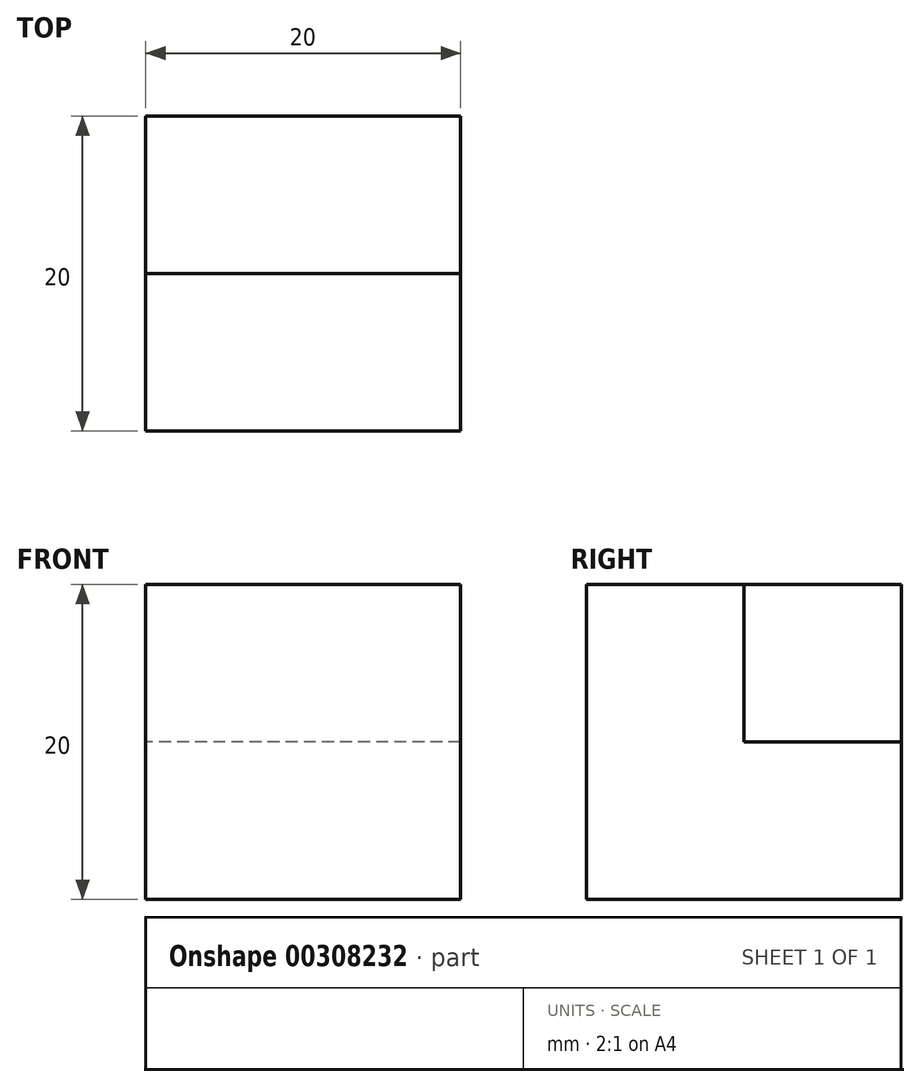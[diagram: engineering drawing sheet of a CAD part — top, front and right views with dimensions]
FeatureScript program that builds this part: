
annotation { "Feature Type Name" : "Feature", "Feature Type Description" : "" }
export const myFeature = defineFeature(function(context is Context, id is Id, definition is map)
    precondition{}
    {
        {
            var Q0;
            Q0=qCreatedBy(makeId("Top.planeOp"),FACE);
            var sketch = newSketch(context, id + "F0", { "sketchPlane" : qUnion([Q0])});
            skLineSegment(sketch, "E0.bottom", {"start": v(9, 10) * mm, "end": v(-11, 10) * mm});
            skLineSegment(sketch, "E0.top", {"start": v(9, 0) * mm, "end": v(-11, 0) * mm});
            skLineSegment(sketch, "E0.left", {"start": v(9, 10) * mm, "end": v(9, 0) * mm});
            skLineSegment(sketch, "E0.right", {"start": v(-11, 10) * mm, "end": v(-11, 0) * mm});
            skLineSegment(sketch, "E1.top", {"start": v(9, -10) * mm, "end": v(-11, -10) * mm});
            skLineSegment(sketch, "E1.left", {"start": v(9, 0) * mm, "end": v(9, -10) * mm});
            skLineSegment(sketch, "E1.right", {"start": v(-11, 0) * mm, "end": v(-11, -10) * mm});
            skSolve(sketch);
        }
        {
            var Q0;
            Q0=makeQuery(id+"F0.imprint","IMPRINT",FACE,{"disambiguationData":[TD([[makeQuery(id+"F0.imprint","IMPRINT",EDGE,{"derivedFrom":sQuery(id+"F0.wireOp",EDGE,"E0.top")}),1.0]])]});
            extrude(context, id + "F1", {"entities" : qUnion([Q0]), "depth" : 20 * mm, "offsetDistance" : 25 * mm});
        }
        {
            var Q0;
            Q0=makeQuery(id+"F0.imprint","IMPRINT",FACE,{"disambiguationData":[TD([[makeQuery(id+"F0.imprint","IMPRINT",EDGE,{"derivedFrom":sQuery(id+"F0.wireOp",EDGE,"E0.bottom")}),1.0]])]});
            extrude(context, id + "F2", {"entities" : qUnion([Q0]), "operationType" : NewBodyOperationType.ADD, "depth" : 10 * mm, "offsetDistance" : 25 * mm});
        }
        {
            var Q0;
            Q0=makeQuery(id+"F2.opExtrude","CAP_FACE",FACE,{"disambiguationData":[OSD([sQuery(id+"F0.wireOp",EDGE,"E0.bottom"),sQuery(id+"F0.wireOp",EDGE,"E0.left"),sQuery(id+"F0.wireOp",EDGE,"E0.right"),sQuery(id+"F0.wireOp",EDGE,"E0.top")])],"isStart":false});
            extrude(context, id + "F3", {"entities" : qUnion([Q0]), "depth" : 10 * mm, "offsetDistance" : 25 * mm});
        }
    });
